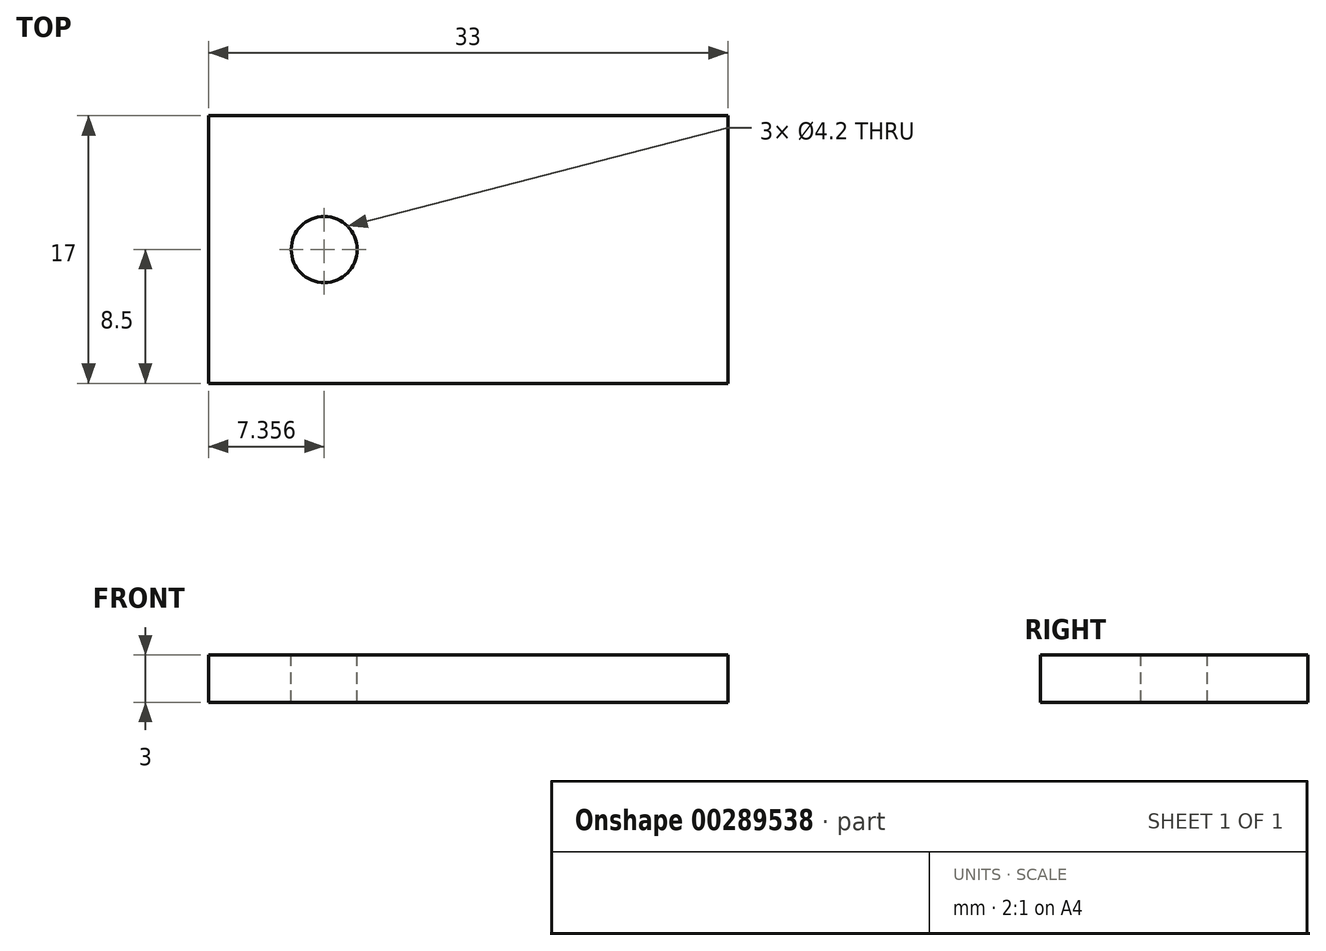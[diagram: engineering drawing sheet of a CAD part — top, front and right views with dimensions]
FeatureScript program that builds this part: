
annotation { "Feature Type Name" : "Feature", "Feature Type Description" : "" }
export const myFeature = defineFeature(function(context is Context, id is Id, definition is map)
    precondition{}
    {
        {
            var Q0;
            Q0=qCreatedBy(makeId("Top.planeOp"),FACE);
            var sketch = newSketch(context, id + "F0", { "sketchPlane" : qUnion([Q0])});
            skLineSegment(sketch, "E0.bottom", {"start": v(16.5, 8.5) * mm, "end": v(-16.5, 8.5) * mm});
            skLineSegment(sketch, "E0.top", {"start": v(16.5, -8.5) * mm, "end": v(-16.5, -8.5) * mm});
            skLineSegment(sketch, "E0.left", {"start": v(16.5, 8.5) * mm, "end": v(16.5, -8.5) * mm});
            skLineSegment(sketch, "E0.right", {"start": v(-16.5, 8.5) * mm, "end": v(-16.5, -8.5) * mm});
            skPoint(sketch, "E0.middle", {"position": v(0, 0) * mm});
            skPoint(sketch, "E1", {"position": v(-9.1, 0) * mm});
            skSolve(sketch);
        }
        {
            var Q0;
            Q0=makeQuery(id+"F0.imprint","IMPRINT",FACE,{"disambiguationData":[TD([[makeQuery(id+"F0.imprint","IMPRINT",EDGE,{"derivedFrom":sQuery(id+"F0.wireOp",EDGE,"E0.bottom")}),1.0]])]});
            extrude(context, id + "F1", {"entities" : qUnion([Q0]), "depth" : 3 * mm});
        }
        {
            var Q0;
            Q0=makeQuery(id+"F1.opExtrude","CAP_FACE",FACE,{"disambiguationData":[OSD([sQuery(id+"F0.wireOp",EDGE,"E0.bottom"),sQuery(id+"F0.wireOp",EDGE,"E0.top"),sQuery(id+"F0.wireOp",EDGE,"E0.left"),sQuery(id+"F0.wireOp",EDGE,"E0.right")])],"isStart":false});
            var sketch = newSketch(context, id + "F2", { "sketchPlane" : qUnion([Q0])});
            skPoint(sketch, "E2", {"position": v(-9.14, 0) * mm});
            skSolve(sketch);
        }
        {
            var Q0;
            Q0=sQuery(id+"F2.wireOp",VERTEX,"E2");
            var Q1;
            Q1=makeQuery(id+"F1.opExtrude","SWEPT_BODY",BODY,{"disambiguationData":[OSD([sQuery(id+"F0.wireOp",EDGE,"E0.bottom"),sQuery(id+"F0.wireOp",EDGE,"E0.top"),sQuery(id+"F0.wireOp",EDGE,"E0.left"),sQuery(id+"F0.wireOp",EDGE,"E0.right")])]});
            hole(context, id + "F3", {"style" : HoleStyle.SIMPLE, "endStyle" : HoleEndStyle.THROUGH, "standardTappedOrClearance" : lookupTablePath({ "standard" : "ISO", "engagement" : "75%", "pitch" : "0.8 mm", "size" : "M5", "type" : "Tapped" }), "standardBlindInLast" : lookupTablePath({ "standard" : "ISO", "engagement" : "75%", "pitch" : "0.8 mm", "size" : "M5", "type" : "Tapped" }), "holeDiameter" : 4.2 * mm, "showTappedDepth" : true, "tappedDepth" : 12 * mm, "tapClearance" : 3, "locations" : qUnion([Q0]), "scope" : qUnion([Q1]), "majorDiameter" : 5 * mm});
        }
    });
